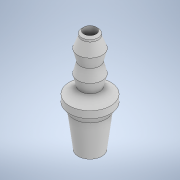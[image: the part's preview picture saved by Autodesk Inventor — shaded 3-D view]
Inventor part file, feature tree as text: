
AUTODESK INVENTOR PART (.ipt)
format: ipt  version: 2021 (Build 250183000, 183)  size: 145,920 bytes
history: native  units: in
note: dims shown in document units (in); Inventor stores cm internally (conversion verified against a paired STEP export)
features: revolve x1, sketch x1
ambient origin geometry x8: Origin, YZ Plane, XZ Plane, XY Plane, X Axis, Y Axis, Z Axis, Center Point
bodies: Solid1 (feature_tree)
feature tree (2):
  revolve  "Revolution1"  [1 undecoded]
  sketch  "Sketch1"  dims[d0=0.5906in d4=0.0394in d5=0.0354in d6=0.0709in d9=0.1969in d10=0.0394in d11=0.0394in d12=0.0984in d14=0.0807in d15=0.0472in d16=0.0709in d17=0.1181in d18=45.0deg d19=0.0118in d20=0.0551in d21=0.0551in d22=0.063in d23=0.063in d24=0.063in d25=0.0481in d26=90.0deg]
note: 1 required parameter value undecoded (feature->parameter linkage not recoverable at this tier; creation-order binding heuristic only, values carry confidence <= 0.55)
